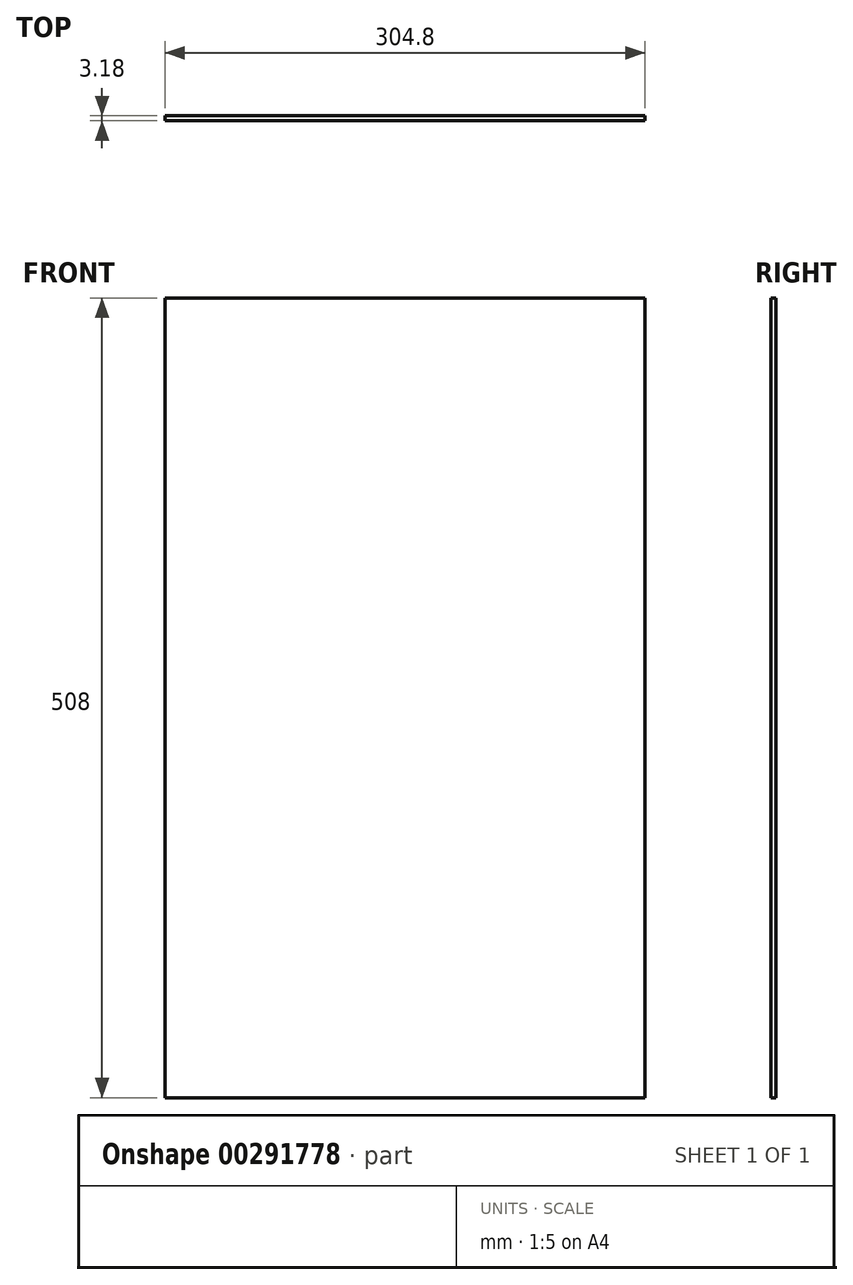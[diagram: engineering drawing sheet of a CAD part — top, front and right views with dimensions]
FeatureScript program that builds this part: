
annotation { "Feature Type Name" : "Feature", "Feature Type Description" : "" }
export const myFeature = defineFeature(function(context is Context, id is Id, definition is map)
    precondition{}
    {
        {
            var Q0;
            Q0=qCreatedBy(makeId("Front.planeOp"),FACE);
            var sketch = newSketch(context, id + "F0", { "sketchPlane" : qUnion([Q0])});
            skLineSegment(sketch, "E0.bottom", {"start": v(-150.44, 265.89) * mm, "end": v(154.36, 265.89) * mm});
            skLineSegment(sketch, "E0.top", {"start": v(-150.44, -242.11) * mm, "end": v(154.36, -242.11) * mm});
            skLineSegment(sketch, "E0.left", {"start": v(-150.44, 265.89) * mm, "end": v(-150.44, -242.11) * mm});
            skLineSegment(sketch, "E0.right", {"start": v(154.36, 265.89) * mm, "end": v(154.36, -242.11) * mm});
            skSolve(sketch);
        }
        {
            var Q0;
            Q0 = qSketchRegion(id + "F0", true);
            extrude(context, id + "F1", {"entities" : qUnion([Q0]), "endBound" : BoundingType.SYMMETRIC, "depth" : 3.17 * mm});
        }
    });
